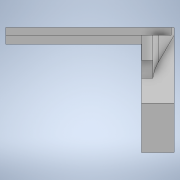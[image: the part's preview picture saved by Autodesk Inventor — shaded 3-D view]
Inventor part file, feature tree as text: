
AUTODESK INVENTOR PART (.ipt)
format: ipt  version: 2022 (Build 260153000, 153)  size: 233,472 bytes
history: native  units: in
note: dims shown in document units (in); Inventor stores cm internally (conversion verified against a paired STEP export)
features: extrude x7, sketch x7, fillet x3
ambient origin geometry x8: Origin, YZ Plane, XZ Plane, XY Plane, X Axis, Y Axis, Z Axis, Center Point
bodies: Solid1 (feature_tree)
feature tree (17):
  extrude  "Extrusion1"  Depth=0.122in
  extrude  "Extrusion2"  Depth=0.1181in
  extrude  "Extrusion3"  Depth=0.2362in TaperAngle=0.0deg
  extrude  "Extrusion4"  Depth=0.0787in
  extrude  "Extrusion5"  Depth=0.315in
  extrude  "Extrusion6"  Depth=0.3937in
  extrude  "Extrusion7"  Depth=0.0787in
  fillet  "Fillet1"  [1 undecoded]
  fillet  "Fillet2"  Radius=0.9843in
  fillet  "Fillet3"  Radius=0.4331in
  sketch  "Sketch1"  dims[d1=0.6693in d2=0.122in]
  sketch  "Sketch2"  dims[d3=0.1181in d4=0.1181in]
  sketch  "Sketch3"  dims[d5=0.2441in d6=0.2362in d7=0.0in]
  sketch  "Sketch4"  dims[d8=0.122in d9=0.0787in]
  sketch  "Sketch6"  dims[d10=0.2362in d11=0.0in d13=0.315in]
  sketch  "Sketch7"  dims[d14=0.3937in d15=0.0in d17=0.5118in]
  sketch  "Sketch8"  dims[d18=0.4921in d19=0.0362in d20=0.0in d21=0.9843in d22=0.4331in d23=0.2165in d24=0.2165in d25=0.1969in d26=0.3937in d27=0.2953in d28=0.1181in d29=0.0787in d30=0.0787in d31=0.0669in d32=0.0in d33=0.4724in d34=0.2756in d35=0.1575in d36=0.0787in d37=0.0787in d38=0.0in d39=0.3543in d40=0.0in d41=0.3543in d42=0.1543in d43=0.4209in d44=0.0in d45=0.0in d46=0.0551in d47=0.0in d48=0.0787in d49=0.2362in d50=0.0787in]
note: 1 required parameter value undecoded (feature->parameter linkage not recoverable at this tier; creation-order binding heuristic only, values carry confidence <= 0.55)
